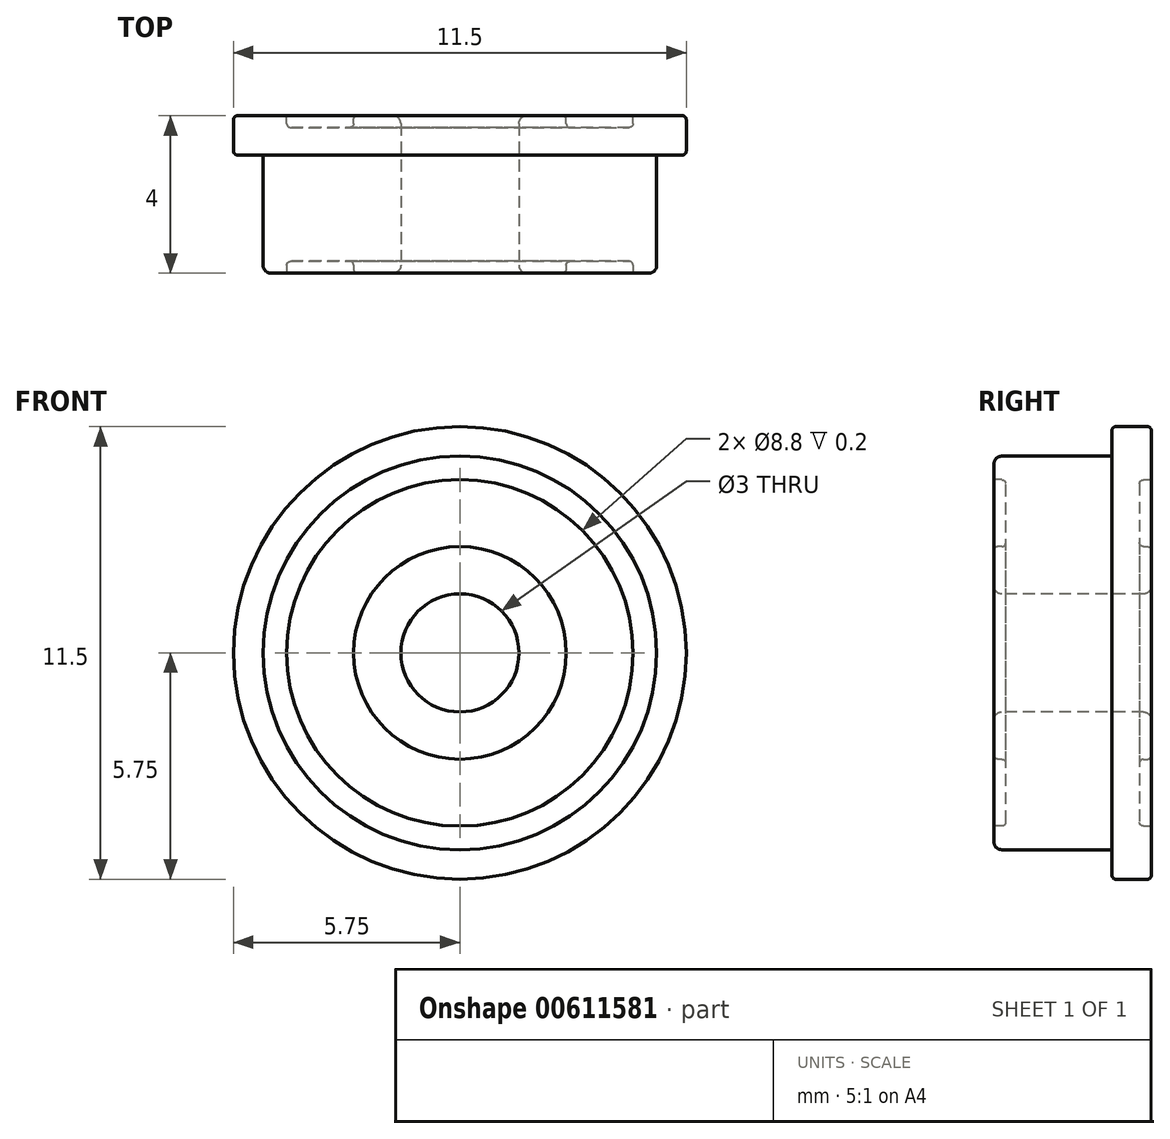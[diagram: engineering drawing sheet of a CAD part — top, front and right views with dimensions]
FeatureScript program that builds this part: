
annotation { "Feature Type Name" : "Feature", "Feature Type Description" : "" }
export const myFeature = defineFeature(function(context is Context, id is Id, definition is map)
    precondition{}
    {
        {
            var Q0;
            Q0=qCreatedBy(makeId("Right.planeOp"),FACE);
            var sketch = newSketch(context, id + "F0", { "sketchPlane" : qUnion([Q0])});
            skLineSegment(sketch, "E0", {"start": v(0, 0) * mm, "end": v(6, 0) * mm, "construction": true});
            skLineSegment(sketch, "E1", {"start": v(-2, 1.5) * mm, "end": v(-2, 5) * mm});
            skLineSegment(sketch, "E2", {"start": v(-2, 5) * mm, "end": v(1, 5) * mm});
            skLineSegment(sketch, "E3", {"start": v(1, 5) * mm, "end": v(1, 5.75) * mm});
            skLineSegment(sketch, "E4", {"start": v(1, 5.75) * mm, "end": v(2, 5.75) * mm});
            skLineSegment(sketch, "E5", {"start": v(2, 5.75) * mm, "end": v(2, 1.5) * mm});
            skLineSegment(sketch, "E6", {"start": v(2, 1.5) * mm, "end": v(-2, 1.5) * mm});
            skLineSegment(sketch, "E7", {"start": v(0, 1.5) * mm, "end": v(0, 0) * mm, "construction": true});
            skSolve(sketch);
        }
        {
            var Q0;
            Q0 = qSketchRegion(id + "F0", true);
            var Q1;
            Q1=sQuery(id+"F0.wireOp",EDGE,"E0");
            revolve(context, id + "F1", {"entities" : qUnion([Q0]), "axis" : qUnion([Q1]), "revolveType" : RevolveType.FULL});
        }
        {
            var Q0;
            Q0=makeQuery(id+"F1.opRevolve","SWEPT_FACE",FACE,{"disambiguationData":[OSD([sQuery(id+"F0.wireOp",EDGE,"E6")])]});
            var Q1;
            Q1=makeQuery(id+"F1.opRevolve","SWEPT_EDGE",EDGE,{"disambiguationData":[OSD([sQuery(id+"F0.wireOp",EDGE,"E1"),sQuery(id+"F0.wireOp",EDGE,"E2")])]});
            fillet(context, id + "F2", {"entities" : qUnion([Q0, Q1]), "radius" : 0.2 * mm, "tangentPropagation" : true, "allowEdgeOverflow" : false});
        }
        {
            var Q0;
            Q0=makeQuery(id+"F1.opRevolve","SWEPT_FACE",FACE,{"disambiguationData":[OSD([sQuery(id+"F0.wireOp",EDGE,"E4")])]});
            fillet(context, id + "F3", {"entities" : qUnion([Q0]), "radius" : 0.1 * mm, "tangentPropagation" : true, "allowEdgeOverflow" : false});
        }
        {
            var Q0;
            Q0=makeQuery(id+"F1.opRevolve","SWEPT_FACE",FACE,{"disambiguationData":[OSD([sQuery(id+"F0.wireOp",EDGE,"E1")])]});
            var sketch = newSketch(context, id + "F4", { "sketchPlane" : qUnion([Q0])});
            skCircle(sketch, "E8.0", {"center": v(0, 0) * mm, "radius": 4.4 * mm});
            skCircle(sketch, "E9.0", {"center": v(0, 0) * mm, "radius": 2.7 * mm});
            skSolve(sketch);
        }
        {
            var Q0;
            Q0 = qSketchRegion(id + "F4", true);
            extrude(context, id + "F5", {"entities" : qUnion([Q0]), "operationType" : NewBodyOperationType.REMOVE, "oppositeDirection" : true, "depth" : 0.3 * mm, "offsetDistance" : 25 * mm});
        }
        {
            var Q0;
            Q0=makeQuery(id+"F1.opRevolve","SWEPT_FACE",FACE,{"disambiguationData":[OSD([sQuery(id+"F0.wireOp",EDGE,"E5")])]});
            var sketch = newSketch(context, id + "F6", { "sketchPlane" : qUnion([Q0])});
            skCircle(sketch, "E10.0", {"center": v(0, 0) * mm, "radius": 4.4 * mm});
            skCircle(sketch, "E11.0", {"center": v(0, 0) * mm, "radius": 2.7 * mm});
            skSolve(sketch);
        }
        {
            var Q0;
            Q0=makeQuery(id+"F6.imprint","IMPRINT",FACE,{"disambiguationData":[TD([[makeQuery(id+"F6.imprint","IMPRINT",EDGE,{"derivedFrom":sQuery(id+"F6.wireOp",EDGE,"E10.0")}),1.0]])]});
            extrude(context, id + "F7", {"entities" : qUnion([Q0]), "operationType" : NewBodyOperationType.REMOVE, "oppositeDirection" : true, "depth" : 0.3 * mm, "offsetDistance" : 25 * mm});
        }
        {
            var Q0;
            Q0=makeQuery(id+"F5.boolean.opBoolean","COPY",FACE,{"derivedFrom":makeQuery(id+"F5.opExtrude","CAP_FACE",FACE,{"disambiguationData":[OSD([sQuery(id+"F4.wireOp",EDGE,"E8.0"),sQuery(id+"F4.wireOp",EDGE,"E9.0")])],"isStart":false})});
            var Q1;
            Q1=makeQuery(id+"F5.boolean.opBoolean","COPY",EDGE,{"derivedFrom":makeQuery(id+"F5.opExtrude","CAP_EDGE",EDGE,{"disambiguationData":[OSD([sQuery(id+"F4.wireOp",EDGE,"E8.0")])],"isStart":true})});
            var Q2;
            Q2=makeQuery(id+"F5.boolean.opBoolean","COPY",EDGE,{"derivedFrom":makeQuery(id+"F5.opExtrude","CAP_EDGE",EDGE,{"disambiguationData":[OSD([sQuery(id+"F4.wireOp",EDGE,"E9.0")])],"isStart":true})});
            var Q3;
            Q3=makeQuery(id+"F7.boolean.opBoolean","COPY",FACE,{"derivedFrom":makeQuery(id+"F7.opExtrude","CAP_FACE",FACE,{"disambiguationData":[OSD([sQuery(id+"F6.wireOp",EDGE,"E10.0"),sQuery(id+"F6.wireOp",EDGE,"E11.0")])],"isStart":false})});
            var Q4;
            Q4=makeQuery(id+"F7.boolean.opBoolean","COPY",EDGE,{"derivedFrom":makeQuery(id+"F7.opExtrude","CAP_EDGE",EDGE,{"disambiguationData":[OSD([sQuery(id+"F6.wireOp",EDGE,"E10.0")])],"isStart":true})});
            var Q5;
            Q5=makeQuery(id+"F7.boolean.opBoolean","COPY",EDGE,{"derivedFrom":makeQuery(id+"F7.opExtrude","CAP_EDGE",EDGE,{"disambiguationData":[OSD([sQuery(id+"F6.wireOp",EDGE,"E11.0")])],"isStart":true})});
            fillet(context, id + "F8", {"entities" : qUnion([Q0, Q1, Q2, Q3, Q4, Q5]), "radius" : 0.1 * mm, "tangentPropagation" : true, "allowEdgeOverflow" : false});
        }
    });
